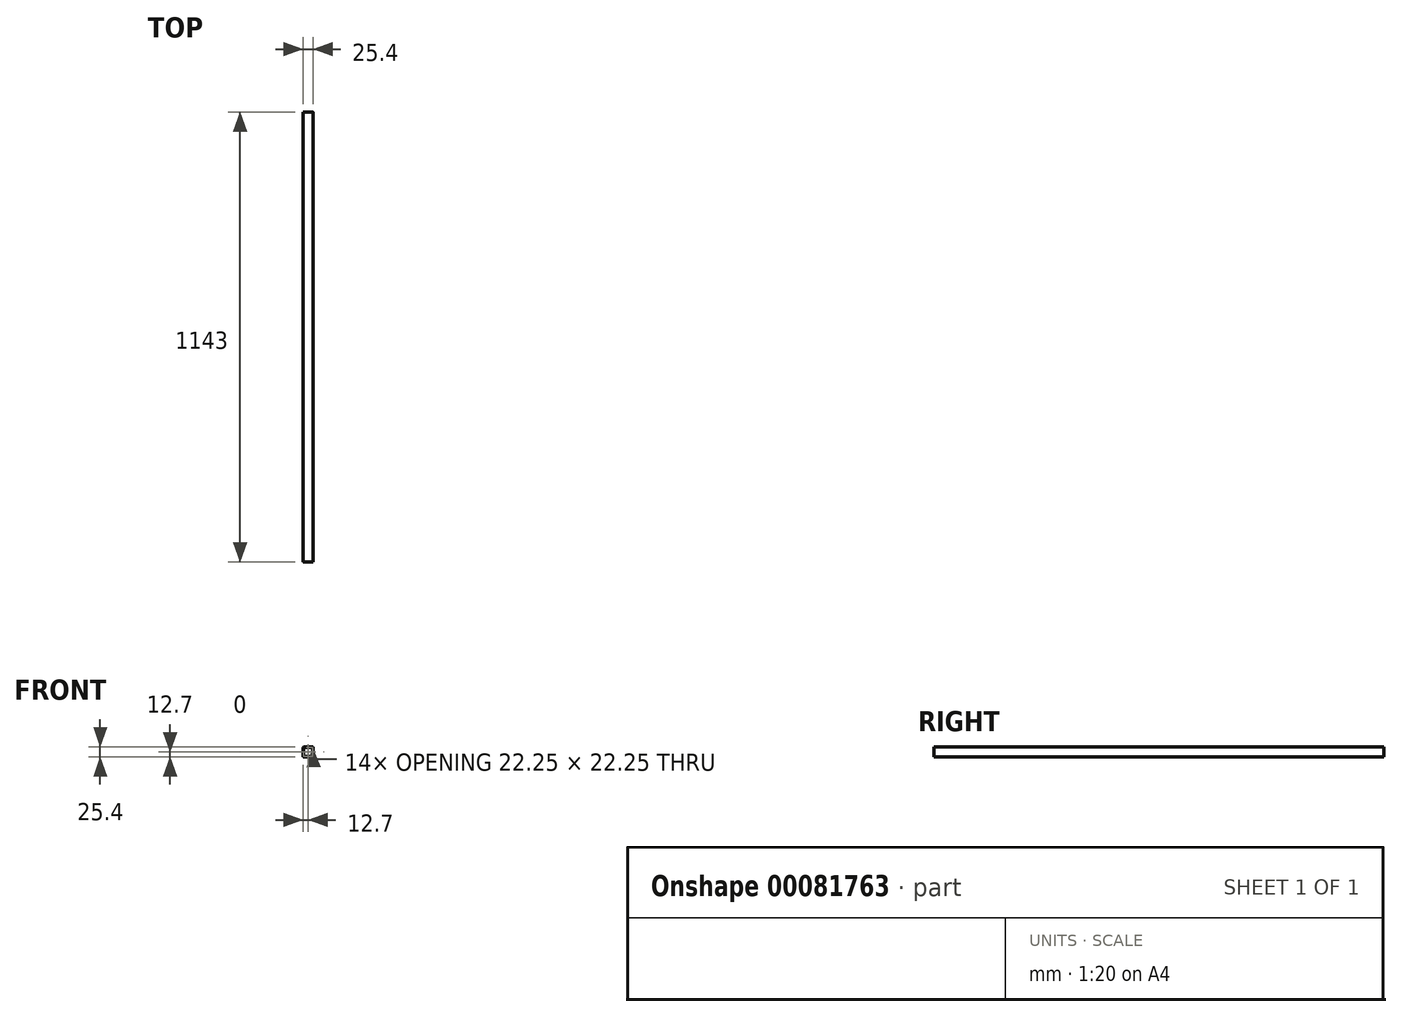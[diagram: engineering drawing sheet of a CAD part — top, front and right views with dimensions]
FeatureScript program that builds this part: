
annotation { "Feature Type Name" : "Feature", "Feature Type Description" : "" }
export const myFeature = defineFeature(function(context is Context, id is Id, definition is map)
    precondition{}
    {
        {
            var Q0;
            Q0=qCreatedBy(makeId("Front.planeOp"),FACE);
            var sketch = newSketch(context, id + "F0", { "sketchPlane" : qUnion([Q0])});
            skLineSegment(sketch, "E0.bottom", {"start": v(-10.62, -12.7) * mm, "end": v(10.62, -12.7) * mm});
            skLineSegment(sketch, "E0.top", {"start": v(-10.62, 12.7) * mm, "end": v(10.62, 12.7) * mm});
            skLineSegment(sketch, "E0.left", {"start": v(-12.7, -10.62) * mm, "end": v(-12.7, 10.62) * mm});
            skLineSegment(sketch, "E0.right", {"start": v(12.7, -10.62) * mm, "end": v(12.7, 10.62) * mm});
            skPoint(sketch, "E0.middle", {"position": v(0, 0) * mm});
            skLineSegment(sketch, "E1.bottom", {"start": v(10.62, -11.13) * mm, "end": v(-10.62, -11.13) * mm});
            skLineSegment(sketch, "E1.top", {"start": v(10.62, 11.13) * mm, "end": v(-10.62, 11.13) * mm});
            skLineSegment(sketch, "E1.left", {"start": v(11.13, -10.62) * mm, "end": v(11.13, 10.62) * mm});
            skLineSegment(sketch, "E1.right", {"start": v(-11.13, -10.62) * mm, "end": v(-11.13, 10.62) * mm});
            skPoint(sketch, "E2.visualSharp", {"position": v(-11.13, 11.13) * mm});
            skArc(sketch, "E2.filletArc", {"start": v(-10.62, 11.13) * mm, "mid": v(-10.98, 10.98) * mm, "end": v(-11.13, 10.62) * mm});
            skPoint(sketch, "E3.visualSharp", {"position": v(11.13, 11.13) * mm});
            skArc(sketch, "E3.filletArc", {"start": v(11.13, 10.62) * mm, "mid": v(10.98, 10.98) * mm, "end": v(10.62, 11.13) * mm});
            skPoint(sketch, "E4.visualSharp", {"position": v(11.13, -11.13) * mm});
            skArc(sketch, "E4.filletArc", {"start": v(10.62, -11.13) * mm, "mid": v(10.98, -10.98) * mm, "end": v(11.13, -10.62) * mm});
            skPoint(sketch, "E5.visualSharp", {"position": v(-11.13, -11.13) * mm});
            skArc(sketch, "E5.filletArc", {"start": v(-11.13, -10.62) * mm, "mid": v(-10.98, -10.98) * mm, "end": v(-10.62, -11.13) * mm});
            skPoint(sketch, "E6.visualSharp", {"position": v(-12.7, 12.7) * mm});
            skArc(sketch, "E6.filletArc", {"start": v(-10.62, 12.7) * mm, "mid": v(-12.09, 12.09) * mm, "end": v(-12.7, 10.62) * mm});
            skPoint(sketch, "E7.visualSharp", {"position": v(12.7, 12.7) * mm});
            skArc(sketch, "E7.filletArc", {"start": v(12.7, 10.62) * mm, "mid": v(12.09, 12.09) * mm, "end": v(10.62, 12.7) * mm});
            skPoint(sketch, "E8.visualSharp", {"position": v(-12.7, -12.7) * mm});
            skArc(sketch, "E8.filletArc", {"start": v(-12.7, -10.62) * mm, "mid": v(-12.09, -12.09) * mm, "end": v(-10.62, -12.7) * mm});
            skPoint(sketch, "E9.visualSharp", {"position": v(12.7, -12.7) * mm});
            skArc(sketch, "E9.filletArc", {"start": v(10.62, -12.7) * mm, "mid": v(12.09, -12.09) * mm, "end": v(12.7, -10.62) * mm});
            skSolve(sketch);
        }
        {
            var Q0;
            Q0 = qSketchRegion(id + "F0", true);
            extrude(context, id + "F1", {"entities" : qUnion([Q0]), "depth" : 1143 * mm, "offsetDistance" : 25.4 * mm});
        }
    });
